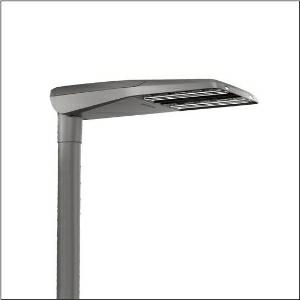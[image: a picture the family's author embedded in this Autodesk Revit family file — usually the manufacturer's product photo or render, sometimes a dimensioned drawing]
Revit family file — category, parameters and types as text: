
# Revit family: streetlight_sl_11_iq_midi___st1_0p1_0_5xc3k51f08me_0ac4
name_source: partatom
category: Lighting Fixtures
units: mm (PartAtom-declared; Revit-internal decimal feet)

## family parameters
Cut with Voids When Loaded = No
Host = Face
Light Source = No
Part Type = Normal
Room Calculation Point = No
Round Connector Dimension = Use Diameter
Shared = No

## types (1)
- --- (1 x LED, 17550 lm, 124.7 W, 3000K)
    Apparent Load = 125 VA
    CIE Flux Codes = 32 65 95 100 100
    Color Rendering = 70
    Color Temperature = 3000K
    Default Elevation = 1800 mm
    Description = Streetlight SL 11 iQ midi, mast luminaire, primary light control with 3 zone facetted reflector, of plastic, silver coated, highly specular, primary optical cover: cover, of PMMA, transparent, light distribution: ST1.0P1.0, light emission: direct distribution, primary light characteristic: asymmetric, installation type: post-top, side-entry, lamps: LED, High Power LED, rated values: 17.550lm | 124,7W | 140,7lm/W (begin service life); end service life: 17.550lm | 132,2W; at 50% lumin. flux: 8.775lm | 57,2W | 153,4lm/W, colour temperature: 3000K, colour rendering: CRI > 70, light colour: 730, light setting 1 begin service life: 100% | 17.550lm | 124,7W | 140,7lm/W | 3.000K, light setting 1 end service life: 132,2W, further light settings possible, control: Street-Remote, Auto-Match, Temp-Guard, Lumen-Switch, Night-Set, Smart-Wire, Light-Fading, Desk-Remote (wireless, voltage-free reading and setting of iQ features in the workshop via application-optimized NFC function/RFID function), optimised constant luminous flux control (CLO 2.0), with cable H07RN-F 5x 1.5mm², mains connection: 230..240V, AC, 50/60Hz, connection cable pre-assembled, cable length: 12,5m, luminaire housing, of diecast aluminium, powder-coated, Siteco® metallic grey (DB 702S), please order mast flange separately, inclination adjustable without tools: 0°, 5°, 10°, 15° (post-top) | 0°, -5°, -10°, -15° (side-entry), sealing non-destructively replaceable, multi-level sealing system, length: 780mm, width: 376mm, height: 118mm, mast flange for spigot size: 42mm (side-entry): 5XC10008XM4, 60/48mm (side-entry/post-top): 5XC10108XM2, 76/60mm (side-entry/post-top): 5XC10108XM1, equipment: Power, protection rating (complete): IP66, insulation class (complete): insulation class II (safety insulation), certification: CE, ENEC, ENEC+, VDE, impact resistance: IK10, permissible operating ambient temperature for outdoor applications: -25..+50°C, standard-compliant lighting for roads and squares, Environmental Product Declaration (EPD) tested and certified by an independent institute, packaging unit: 1 piece

Light Distribution: ST1.0P1.0
    Height = 118 mm
    Lamp = 1 x LED
    Lamp Light Flux = 17550 lm
    Lamp Power = 124.7 W
    Lamp count = 1
    Length = 780 mm
    Luminous efficacy = 141 lm/W
    Manufacturer = Siteco
    ModVariant = No
    Model = 5XC3K51F08ME
    Number of Poles = 1
    OnlyDefault = Yes
    Power Factor = 1
    Product Name = Streetlight SL 11 iQ midi | ST1.0P1.0
    Product group = mast luminaire | pylon top
    ProductGroupID = 6100
    Protection Class = Protection class II
    Protection Degree = IP 66
    RLX_Detail_Level = 1
    RLX_Emergency_Light_Flux = 0 lm
    RLX_Emergency_Type = 0
    RLX_Emergency_Type_DB = No
    RlxData = <blob elided: 70949 chars, md5=ccb90974>
    Socket = socket
    Standby Power = 0 W
    System Light Flux = 17550 lm
    System Power = 125 W
    Type Comments = factory setting: luminous flux: 100 % | dim-lin: 254 | 557 mA
    Type Image = l_1005960.jpg
    URL = http://relux.com
    VarID = @adj_061473
    Voltage = 0 V
    Weight = 0.00 kg
    Width = 376 mm

## geometry (parser evidence)
native form markers: Blend x4, Sweep x8
no freeform markers — native parametric forms only
